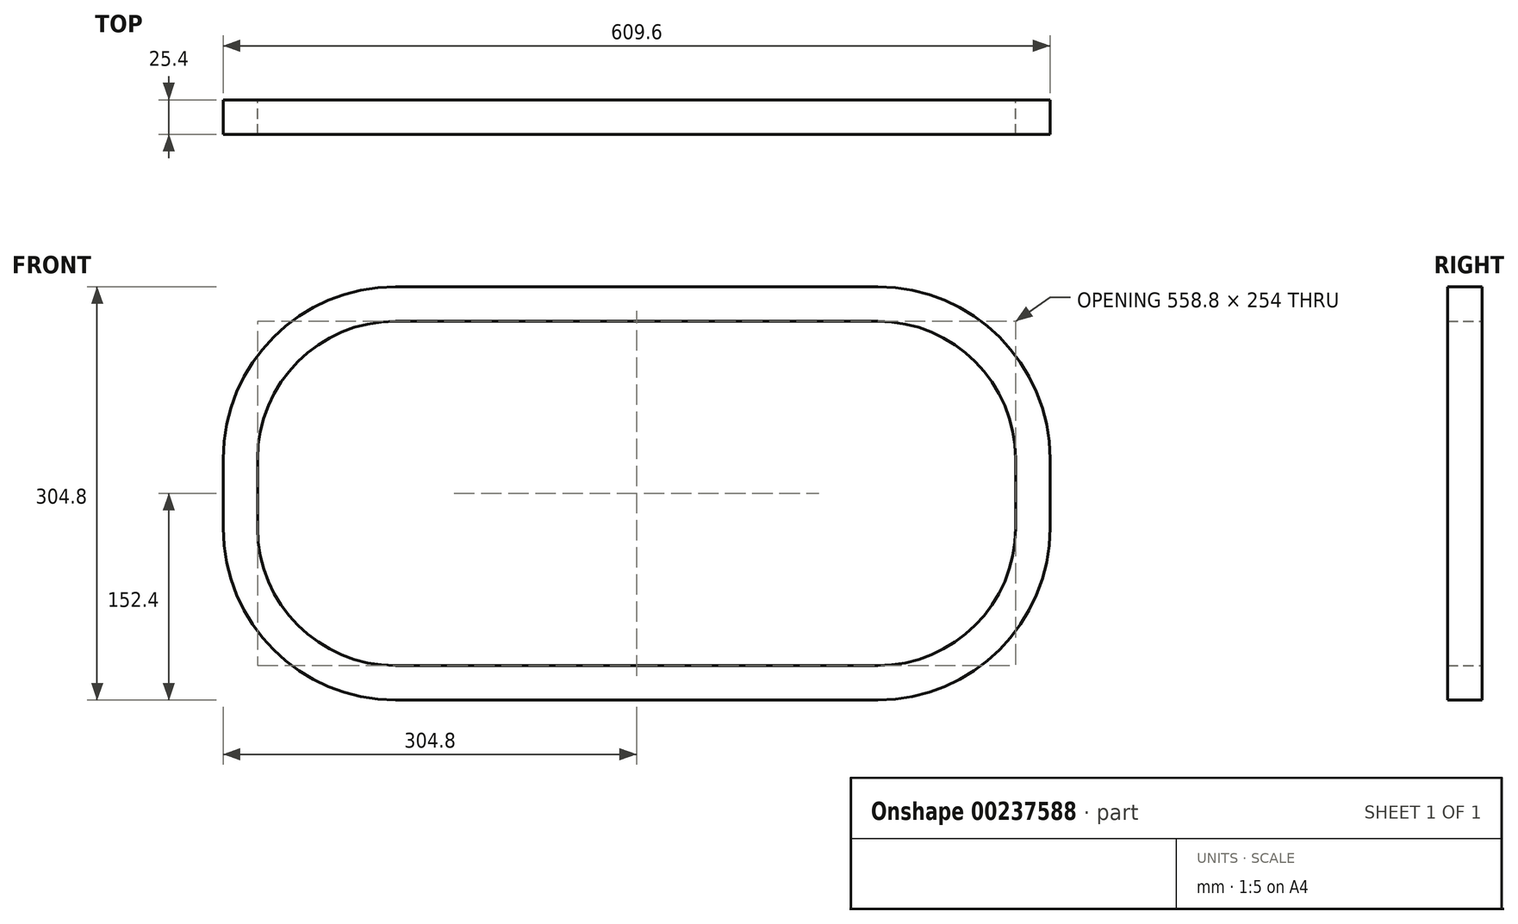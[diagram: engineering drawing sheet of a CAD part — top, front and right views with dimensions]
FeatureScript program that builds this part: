
annotation { "Feature Type Name" : "Feature", "Feature Type Description" : "" }
export const myFeature = defineFeature(function(context is Context, id is Id, definition is map)
    precondition{}
    {
        {
            var Q0;
            Q0=qCreatedBy(makeId("Front.planeOp"),FACE);
            var sketch = newSketch(context, id + "F0", { "sketchPlane" : qUnion([Q0])});
            skLineSegment(sketch, "E0.bottom", {"start": v(177.8, 152.4) * mm, "end": v(-177.8, 152.4) * mm});
            skLineSegment(sketch, "E0.top", {"start": v(177.8, -152.4) * mm, "end": v(-177.8, -152.4) * mm});
            skLineSegment(sketch, "E0.left", {"start": v(304.8, 25.4) * mm, "end": v(304.8, -25.4) * mm});
            skLineSegment(sketch, "E0.right", {"start": v(-304.8, 25.4) * mm, "end": v(-304.8, -25.4) * mm});
            skPoint(sketch, "E0.middle", {"position": v(0, 0) * mm});
            skPoint(sketch, "E1.visualSharp", {"position": v(-304.8, 152.4) * mm});
            skArc(sketch, "E1.filletArc", {"start": v(-177.8, 152.4) * mm, "mid": v(-267.6, 115.2) * mm, "end": v(-304.8, 25.4) * mm});
            skPoint(sketch, "E2.visualSharp", {"position": v(-304.8, -152.4) * mm});
            skArc(sketch, "E2.filletArc", {"start": v(-304.8, -25.4) * mm, "mid": v(-267.6, -115.2) * mm, "end": v(-177.8, -152.4) * mm});
            skPoint(sketch, "E3.visualSharp", {"position": v(304.8, 152.4) * mm});
            skArc(sketch, "E3.filletArc", {"start": v(304.8, 25.4) * mm, "mid": v(267.6, 115.2) * mm, "end": v(177.8, 152.4) * mm});
            skPoint(sketch, "E4.visualSharp", {"position": v(304.8, -152.4) * mm});
            skArc(sketch, "E4.filletArc", {"start": v(177.8, -152.4) * mm, "mid": v(267.6, -115.2) * mm, "end": v(304.8, -25.4) * mm});
            skSolve(sketch);
        }
        {
            var Q0;
            Q0=makeQuery(id+"F0.imprint","IMPRINT",FACE,{"disambiguationData":[TD([[makeQuery(id+"F0.imprint","IMPRINT",EDGE,{"derivedFrom":sQuery(id+"F0.wireOp",EDGE,"E0.bottom")}),1.0]])]});
            var sketch = newSketch(context, id + "F1", { "sketchPlane" : qUnion([Q0])});
            skArc(sketch, "E5.0", {"start": v(279.4, 25.4) * mm, "mid": v(249.64, 97.24) * mm, "end": v(177.8, 127) * mm});
            skLineSegment(sketch, "E5.1", {"start": v(279.4, 25.4) * mm, "end": v(279.4, -25.4) * mm});
            skLineSegment(sketch, "E5.2", {"start": v(177.8, 127) * mm, "end": v(-177.8, 127) * mm});
            skArc(sketch, "E5.3", {"start": v(177.8, -127) * mm, "mid": v(249.64, -97.24) * mm, "end": v(279.4, -25.4) * mm});
            skArc(sketch, "E5.4", {"start": v(-177.8, 127) * mm, "mid": v(-249.64, 97.24) * mm, "end": v(-279.4, 25.4) * mm});
            skLineSegment(sketch, "E5.5", {"start": v(-279.4, 25.4) * mm, "end": v(-279.4, -25.4) * mm});
            skArc(sketch, "E5.6", {"start": v(-279.4, -25.4) * mm, "mid": v(-249.64, -97.24) * mm, "end": v(-177.8, -127) * mm});
            skLineSegment(sketch, "E5.7", {"start": v(177.8, -127) * mm, "end": v(-177.8, -127) * mm});
            skSolve(sketch);
        }
        {
            var Q0;
            Q0=makeQuery(id+"F1.imprint","IMPRINT",FACE,{"disambiguationData":[TD([[makeQuery(id+"F1.imprint","IMPRINT",EDGE,{"derivedFrom":sQuery(id+"F1.wireOp",EDGE,"E5.0")}),-1.0]])]});
            extrude(context, id + "F2", {"entities" : qUnion([Q0]), "depth" : 25.4 * mm});
        }
    });
